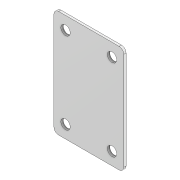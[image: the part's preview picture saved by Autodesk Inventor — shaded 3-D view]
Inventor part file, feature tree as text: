
AUTODESK INVENTOR PART (.ipt)
format: ipt  version: 2020 (Build 240168000, 168)  size: 101,376 bytes
history: native  units: mm
features: other x1, extrude x1, fillet x1, sketch x1
ambient origin geometry x8: Origin, YZ Plane, XZ Plane, XY Plane, X Axis, Y Axis, Z Axis, Center Point
bodies: Body1 (feature_tree)
feature tree (4):
  other  "솔리드1"
  extrude  "돌출1"  Depth=30.0mm
  fillet  "모깎기1"  Radius=46.0mm
  sketch  "스케치1"
